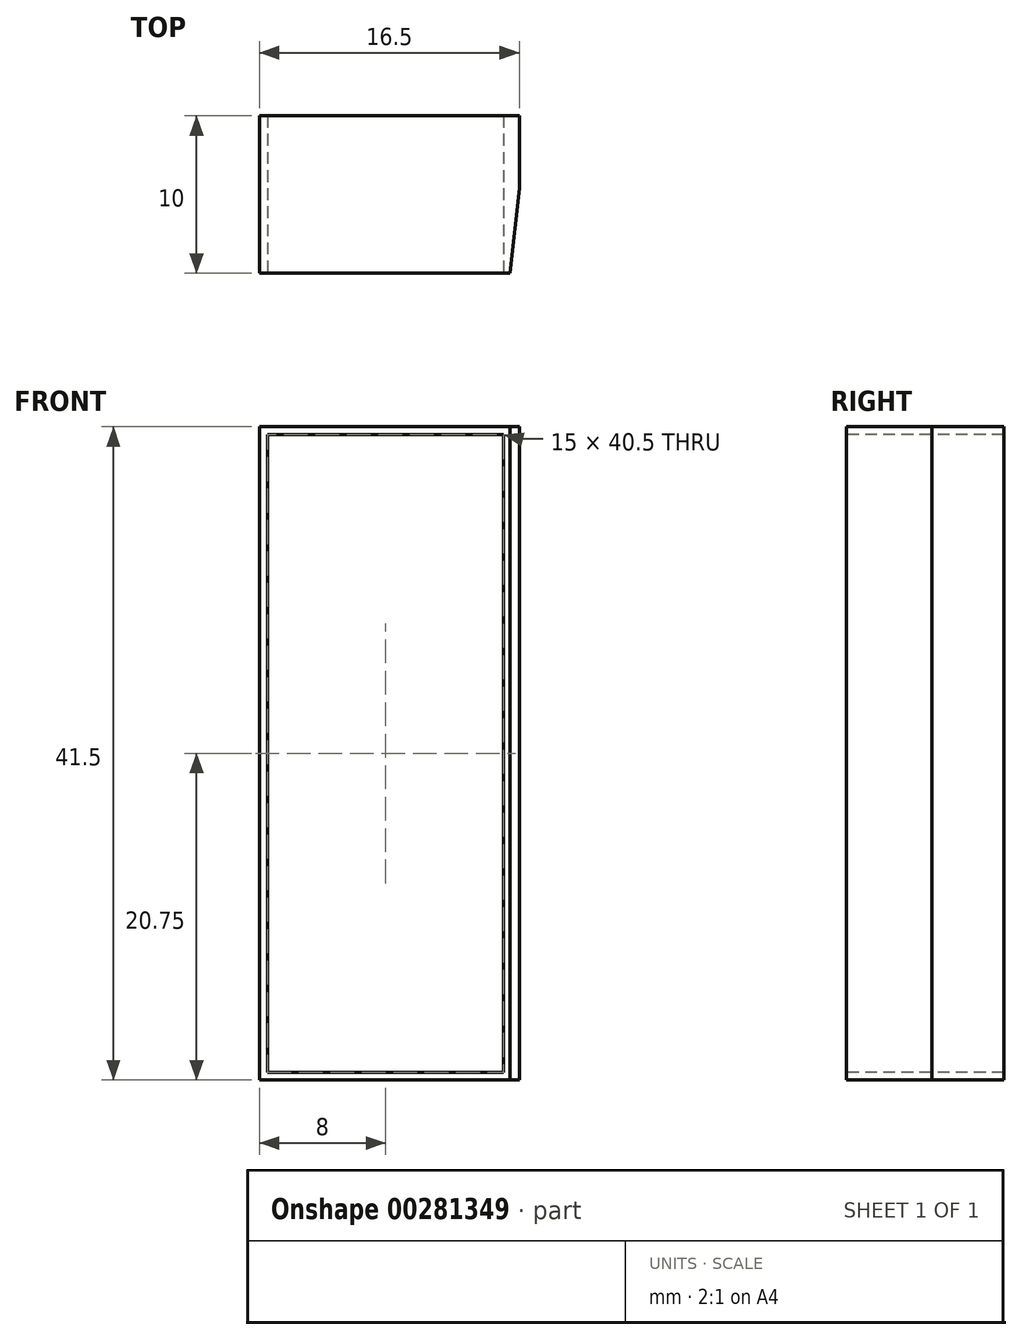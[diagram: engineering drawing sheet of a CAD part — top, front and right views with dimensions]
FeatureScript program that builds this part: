
annotation { "Feature Type Name" : "Feature", "Feature Type Description" : "" }
export const myFeature = defineFeature(function(context is Context, id is Id, definition is map)
    precondition{}
    {
        {
            var Q0;
            Q0=qCreatedBy(makeId("Front.planeOp"),FACE);
            var sketch = newSketch(context, id + "F0", { "sketchPlane" : qUnion([Q0])});
            skLineSegment(sketch, "E0.bottom", {"start": v(8.25, 20.75) * mm, "end": v(-8.25, 20.75) * mm});
            skLineSegment(sketch, "E0.top", {"start": v(8.25, -20.75) * mm, "end": v(-8.25, -20.75) * mm});
            skLineSegment(sketch, "E0.left", {"start": v(8.25, 20.75) * mm, "end": v(8.25, -20.75) * mm});
            skLineSegment(sketch, "E0.right", {"start": v(-8.25, 20.75) * mm, "end": v(-8.25, -20.75) * mm});
            skPoint(sketch, "E0.middle", {"position": v(0, 0) * mm});
            skSolve(sketch);
        }
        {
            var Q0;
            Q0 = qSketchRegion(id + "F0", true);
            extrude(context, id + "F1", {"entities" : qUnion([Q0]), "endBound" : BoundingType.SYMMETRIC, "depth" : 10 * mm});
        }
        {
            var Q0;
            Q0=qCreatedBy(makeId("Front.planeOp"),FACE);
            var sketch = newSketch(context, id + "F2", { "sketchPlane" : qUnion([Q0])});
            skLineSegment(sketch, "E1.bottom", {"start": v(7.25, 20.25) * mm, "end": v(-7.75, 20.25) * mm});
            skLineSegment(sketch, "E1.top", {"start": v(7.25, -20.25) * mm, "end": v(-7.75, -20.25) * mm});
            skLineSegment(sketch, "E1.left", {"start": v(7.25, 20.25) * mm, "end": v(7.25, -20.25) * mm});
            skLineSegment(sketch, "E1.right", {"start": v(-7.75, 20.25) * mm, "end": v(-7.75, -20.25) * mm});
            skPoint(sketch, "E1.middle", {"position": v(-0.25, 0) * mm});
            skSolve(sketch);
        }
        {
            var Q0;
            Q0 = qSketchRegion(id + "F2", true);
            extrude(context, id + "F3", {"entities" : qUnion([Q0]), "operationType" : NewBodyOperationType.REMOVE, "endBound" : BoundingType.SYMMETRIC, "oppositeDirection" : true, "depth" : 25 * mm});
        }
        {
            var Q0;
            Q0=qCreatedBy(makeId("Top.planeOp"),FACE);
            var sketch = newSketch(context, id + "F4", { "sketchPlane" : qUnion([Q0])});
            skLineSegment(sketch, "E2", {"start": v(8.27, 0.58) * mm, "end": v(7.6, -5.69) * mm});
            skLineSegment(sketch, "E3", {"start": v(8.27, 0.58) * mm, "end": v(10.65, 0.32) * mm});
            skLineSegment(sketch, "E4", {"start": v(10.65, 0.32) * mm, "end": v(10.65, -6.16) * mm});
            skLineSegment(sketch, "E5", {"start": v(10.65, -6.16) * mm, "end": v(7.6, -5.69) * mm});
            skSolve(sketch);
        }
        {
            var Q0;
            Q0 = qSketchRegion(id + "F4", true);
            extrude(context, id + "F5", {"entities" : qUnion([Q0]), "operationType" : NewBodyOperationType.REMOVE, "endBound" : BoundingType.SYMMETRIC, "oppositeDirection" : true, "depth" : 45.6 * mm});
        }
    });
